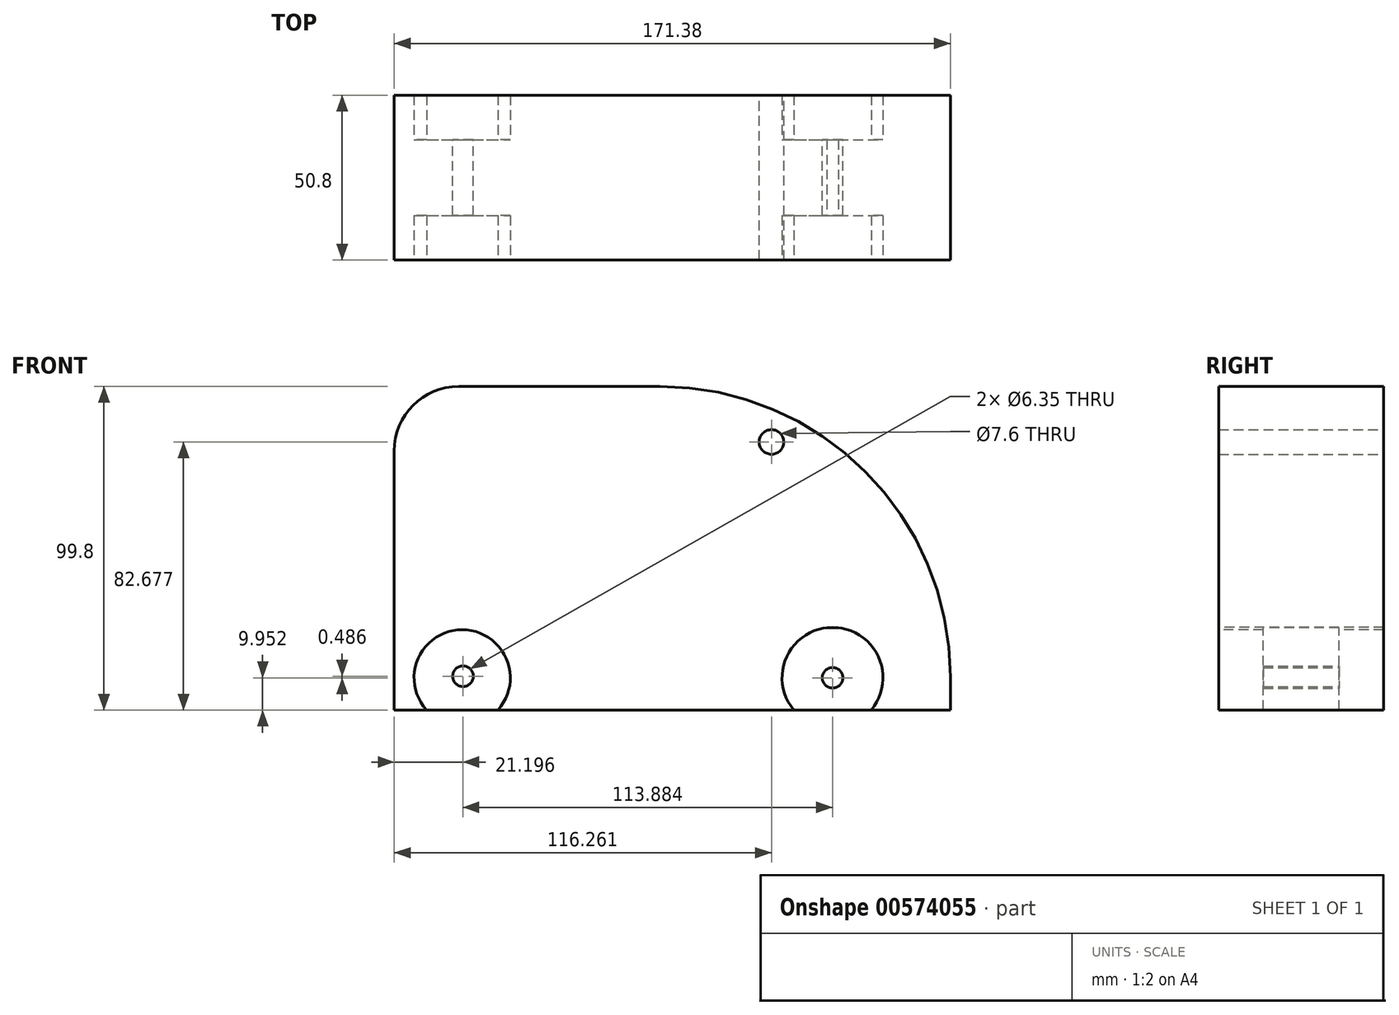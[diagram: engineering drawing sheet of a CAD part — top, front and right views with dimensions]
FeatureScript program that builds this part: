
annotation { "Feature Type Name" : "Feature", "Feature Type Description" : "" }
export const myFeature = defineFeature(function(context is Context, id is Id, definition is map)
    precondition{}
    {
        {
            var Q0;
            Q0=qCreatedBy(makeId("Front.planeOp"),FACE);
            var sketch = newSketch(context, id + "F0", { "sketchPlane" : qUnion([Q0])});
            skLineSegment(sketch, "E0.bottom", {"start": v(-79.37, 46.99) * mm, "end": v(-17.42, 46.99) * mm});
            skLineSegment(sketch, "E0.top", {"start": v(-99.26, -52.81) * mm, "end": v(72.12, -52.81) * mm});
            skLineSegment(sketch, "E0.left", {"start": v(-99.26, 27.1) * mm, "end": v(-99.26, -52.81) * mm});
            skLineSegment(sketch, "E0.right", {"start": v(72.12, -42.55) * mm, "end": v(72.12, -52.81) * mm});
            skPoint(sketch, "E1.visualSharp", {"position": v(-99.26, 46.99) * mm});
            skArc(sketch, "E1.filletArc", {"start": v(-79.37, 46.99) * mm, "mid": v(-93.44, 41.16) * mm, "end": v(-99.26, 27.1) * mm});
            skPoint(sketch, "E2.visualSharp", {"position": v(72.12, 46.99) * mm});
            skArc(sketch, "E2.filletArc", {"start": v(72.12, -42.55) * mm, "mid": v(45.9, 20.76) * mm, "end": v(-17.42, 46.99) * mm});
            skCircle(sketch, "E3", {"center": v(17, 29.87) * mm, "radius": 3.8 * mm});
            skSolve(sketch);
        }
        {
            var Q0;
            Q0=makeQuery(id+"F0.imprint","IMPRINT",FACE,{"disambiguationData":[TD([[makeQuery(id+"F0.imprint","IMPRINT",EDGE,{"derivedFrom":sQuery(id+"F0.wireOp",EDGE,"E0.bottom")}),-1.0]])]});
            extrude(context, id + "F1", {"entities" : qUnion([Q0]), "depth" : 50.8 * mm, "offsetDistance" : 25.4 * mm});
        }
        {
            var Q0;
            Q0=makeQuery(id+"F1.opExtrude","CAP_FACE",FACE,{"disambiguationData":[OSD([sQuery(id+"F0.wireOp",EDGE,"E0.bottom"),sQuery(id+"F0.wireOp",EDGE,"E0.top"),sQuery(id+"F0.wireOp",EDGE,"E0.left"),sQuery(id+"F0.wireOp",EDGE,"E0.right"),sQuery(id+"F0.wireOp",EDGE,"E1.filletArc"),sQuery(id+"F0.wireOp",EDGE,"E2.filletArc")])],"isStart":false});
            var sketch = newSketch(context, id + "F2", { "sketchPlane" : qUnion([Q0])});
            skCircle(sketch, "E4", {"center": v(-78.3, -42.86) * mm, "radius": 14.83 * mm});
            skCircle(sketch, "E5", {"center": v(35.82, -42.86) * mm, "radius": 15.54 * mm});
            skSolve(sketch);
        }
        {
            var Q0;
            Q0=sQuery(id+"F2.wireOp",VERTEX,"E4.center");
            var Q1;
            Q1=sQuery(id+"F2.wireOp",VERTEX,"E5.center");
            var Q2;
            Q2=makeQuery(id+"F1.opExtrude","SWEPT_BODY",BODY,{"disambiguationData":[OSD([sQuery(id+"F0.wireOp",EDGE,"E0.bottom"),sQuery(id+"F0.wireOp",EDGE,"E0.top"),sQuery(id+"F0.wireOp",EDGE,"E0.left"),sQuery(id+"F0.wireOp",EDGE,"E0.right"),sQuery(id+"F0.wireOp",EDGE,"E1.filletArc"),sQuery(id+"F0.wireOp",EDGE,"E2.filletArc")])]});
            hole(context, id + "F3", {"style" : HoleStyle.SIMPLE, "endStyle" : HoleEndStyle.THROUGH, "holeDiameter" : 6.35 * mm, "isTappedThrough" : true, "tappedDepth" : 12.7 * mm, "tapClearance" : 3, "locations" : qUnion([Q0, Q1]), "scope" : qUnion([Q2])});
        }
        {
            var Q0;
            Q0 = qSketchRegion(id + "F2", true);
            extrude(context, id + "F4", {"entities" : qUnion([Q0]), "operationType" : NewBodyOperationType.REMOVE, "oppositeDirection" : true, "depth" : 50.8 * mm, "offsetDistance" : 25.4 * mm});
        }
        {
            var Q0;
            {var subQ0=sQuery(id+"F0.wireOp",EDGE,"E2.filletArc");var subQ1=sQuery(id+"F0.wireOp",EDGE,"E1.filletArc");var subQ2=sQuery(id+"F0.wireOp",EDGE,"E0.right");var subQ3=sQuery(id+"F0.wireOp",EDGE,"E0.left");var subQ4=sQuery(id+"F0.wireOp",EDGE,"E0.top");var subQ5=sQuery(id+"F0.wireOp",EDGE,"E0.bottom");Q0=makeQuery(id+"F4.boolean.opBoolean","SPLIT",FACE,{"disambiguationData":[TD([makeQuery(id+"F1.opExtrude","CAP_FACE",FACE,{"disambiguationData":[OSD([subQ5,subQ4,subQ3,subQ2,subQ1,subQ0])],"isStart":true}),makeQuery(id+"F1.opExtrude","CAP_FACE",FACE,{"disambiguationData":[OSD([subQ5,subQ4,subQ3,subQ2,subQ1,subQ0])],"isStart":false}),makeQuery(id+"F4.opExtrude","SWEPT_FACE",FACE,{"disambiguationData":[OSD([sQuery(id+"F2.wireOp",EDGE,"E4")])]}),makeQuery(id+"F4.opExtrude","SWEPT_FACE",FACE,{"disambiguationData":[OSD([sQuery(id+"F2.wireOp",EDGE,"E5")])]})])],"derivedFrom":makeQuery(id+"F1.opExtrude","SWEPT_FACE",FACE,{"disambiguationData":[OSD([subQ4])]})});}
            var sketch = newSketch(context, id + "F5", { "sketchPlane" : qUnion([Q0])});
            skLineSegment(sketch, "E6.right", {"start": v(23.88, 18.1) * mm, "end": v(23.88, 35.82) * mm});
            skLineSegment(sketch, "E7.left", {"start": v(-67.32, 17.85) * mm, "end": v(-67.32, 35.09) * mm});
            skLineSegment(sketch, "E7.right", {"start": v(-89.72, 17.85) * mm, "end": v(-89.72, 35.09) * mm});
            skLineSegment(sketch, "E8.bottom", {"start": v(23.88, 13.78) * mm, "end": v(55, 13.78) * mm});
            skLineSegment(sketch, "E8.top", {"start": v(23.88, 37.09) * mm, "end": v(55, 37.09) * mm});
            skLineSegment(sketch, "E8.left", {"start": v(23.88, 13.78) * mm, "end": v(23.88, 37.09) * mm});
            skLineSegment(sketch, "E8.right", {"start": v(55, 13.78) * mm, "end": v(55, 37.09) * mm});
            skLineSegment(sketch, "E9.bottom", {"start": v(23.88, 22.27) * mm, "end": v(9.84, 22.27) * mm});
            skLineSegment(sketch, "E9.top", {"start": v(23.88, 37.09) * mm, "end": v(9.84, 37.09) * mm});
            skLineSegment(sketch, "E9.left", {"start": v(23.88, 22.27) * mm, "end": v(23.88, 37.09) * mm});
            skLineSegment(sketch, "E9.right", {"start": v(9.84, 22.27) * mm, "end": v(9.84, 37.09) * mm});
            skLineSegment(sketch, "E10.bottom", {"start": v(23.88, 13.78) * mm, "end": v(9.84, 13.78) * mm});
            skLineSegment(sketch, "E10.left", {"start": v(23.88, 13.78) * mm, "end": v(23.88, 22.27) * mm});
            skLineSegment(sketch, "E10.right", {"start": v(9.84, 13.78) * mm, "end": v(9.84, 22.27) * mm});
            skPoint(sketch, "E11.firstSnap0", {"position": v(16.86, 13.78) * mm});
            skLineSegment(sketch, "E11.bottom", {"start": v(-67.32, 13.78) * mm, "end": v(-96.76, 13.78) * mm});
            skLineSegment(sketch, "E11.top", {"start": v(-67.32, 37.09) * mm, "end": v(-96.76, 37.09) * mm});
            skLineSegment(sketch, "E11.left", {"start": v(-67.32, 13.78) * mm, "end": v(-67.32, 37.09) * mm});
            skLineSegment(sketch, "E11.right", {"start": v(-96.76, 13.78) * mm, "end": v(-96.76, 37.09) * mm});
            skLineSegment(sketch, "E12.bottom", {"start": v(-67.32, 13.78) * mm, "end": v(-55, 13.78) * mm});
            skLineSegment(sketch, "E12.top", {"start": v(-67.32, 37.09) * mm, "end": v(-55, 37.09) * mm});
            skLineSegment(sketch, "E12.right", {"start": v(-55, 13.78) * mm, "end": v(-55, 37.09) * mm});
            skSolve(sketch);
        }
        {
            var Q0;
            {var subQ5=sQuery(id+"F5.wireOp",EDGE,"E8.bottom");Q0=makeQuery(id+"F5.imprint","IMPRINT",FACE,{"disambiguationData":[TD([[makeQuery(id+"F5.imprint","IMPRINT",EDGE,{"derivedFrom":subQ5}),1.0]])]});}
            var Q1;
            {var subQ1=sQuery(id+"F5.wireOp",EDGE,"E9.top");Q1=makeQuery(id+"F5.imprint","IMPRINT",FACE,{"disambiguationData":[TD([[makeQuery(id+"F5.imprint","IMPRINT",EDGE,{"derivedFrom":subQ1}),1.0]])]});}
            var Q2;
            {var subQ3=sQuery(id+"F5.wireOp",EDGE,"E10.bottom");Q2=makeQuery(id+"F5.imprint","IMPRINT",FACE,{"disambiguationData":[TD([[makeQuery(id+"F5.imprint","IMPRINT",EDGE,{"derivedFrom":subQ3}),-1.0]])]});}
            var Q3;
            {var subQ3=sQuery(id+"F5.wireOp",EDGE,"E12.bottom");Q3=makeQuery(id+"F5.imprint","IMPRINT",FACE,{"disambiguationData":[TD([[makeQuery(id+"F5.imprint","IMPRINT",EDGE,{"derivedFrom":subQ3}),1.0]])]});}
            var Q4;
            {var subQ2=sQuery(id+"F5.wireOp",EDGE,"E11.bottom");Q4=makeQuery(id+"F5.imprint","IMPRINT",FACE,{"disambiguationData":[TD([[makeQuery(id+"F5.imprint","IMPRINT",EDGE,{"derivedFrom":subQ2}),-1.0]])]});}
            extrude(context, id + "F6", {"entities" : qUnion([Q0, Q1, Q2, Q3, Q4]), "operationType" : NewBodyOperationType.ADD, "oppositeDirection" : true, "depth" : 25.4 * mm, "offsetDistance" : 25.4 * mm});
        }
        {
            var Q0;
            Q0=makeQuery(id+"F6.opExtrude","SWEPT_FACE",FACE,{"disambiguationData":[OSD([sQuery(id+"F5.wireOp",EDGE,"E8.bottom"),sQuery(id+"F5.wireOp",EDGE,"E10.bottom")])]});
            var sketch = newSketch(context, id + "F7", { "sketchPlane" : qUnion([Q0])});
            skCircle(sketch, "E13", {"center": v(-35.82, -42.86) * mm, "radius": 1.77 * mm});
            skCircle(sketch, "E14", {"center": v(78.06, -42.37) * mm, "radius": 2.5 * mm});
            skSolve(sketch);
        }
        {
            var Q0;
            Q0=sQuery(id+"F7.wireOp",VERTEX,"E13.center");
            var Q1;
            Q1=makeQuery(id+"F1.opExtrude","SWEPT_BODY",BODY,{"disambiguationData":[OSD([sQuery(id+"F0.wireOp",EDGE,"E0.bottom"),sQuery(id+"F0.wireOp",EDGE,"E0.top"),sQuery(id+"F0.wireOp",EDGE,"E0.left"),sQuery(id+"F0.wireOp",EDGE,"E0.right"),sQuery(id+"F0.wireOp",EDGE,"E1.filletArc"),sQuery(id+"F0.wireOp",EDGE,"E2.filletArc")])]});
            hole(context, id + "F8", {"style" : HoleStyle.SIMPLE, "endStyle" : HoleEndStyle.THROUGH, "holeDiameter" : 6.35 * mm, "isTappedThrough" : true, "tappedDepth" : 12.7 * mm, "tapClearance" : 3, "locations" : qUnion([Q0]), "scope" : qUnion([Q1])});
        }
        {
            var Q0;
            Q0=sQuery(id+"F7.wireOp",VERTEX,"E14.center");
            var Q1;
            Q1=makeQuery(id+"F1.opExtrude","SWEPT_BODY",BODY,{"disambiguationData":[OSD([sQuery(id+"F0.wireOp",EDGE,"E0.bottom"),sQuery(id+"F0.wireOp",EDGE,"E0.top"),sQuery(id+"F0.wireOp",EDGE,"E0.left"),sQuery(id+"F0.wireOp",EDGE,"E0.right"),sQuery(id+"F0.wireOp",EDGE,"E1.filletArc"),sQuery(id+"F0.wireOp",EDGE,"E2.filletArc")])]});
            hole(context, id + "F9", {"style" : HoleStyle.SIMPLE, "endStyle" : HoleEndStyle.THROUGH, "holeDiameter" : 6.35 * mm, "isTappedThrough" : true, "tappedDepth" : 12.7 * mm, "tapClearance" : 3, "locations" : qUnion([Q0]), "scope" : qUnion([Q1])});
        }
    });
